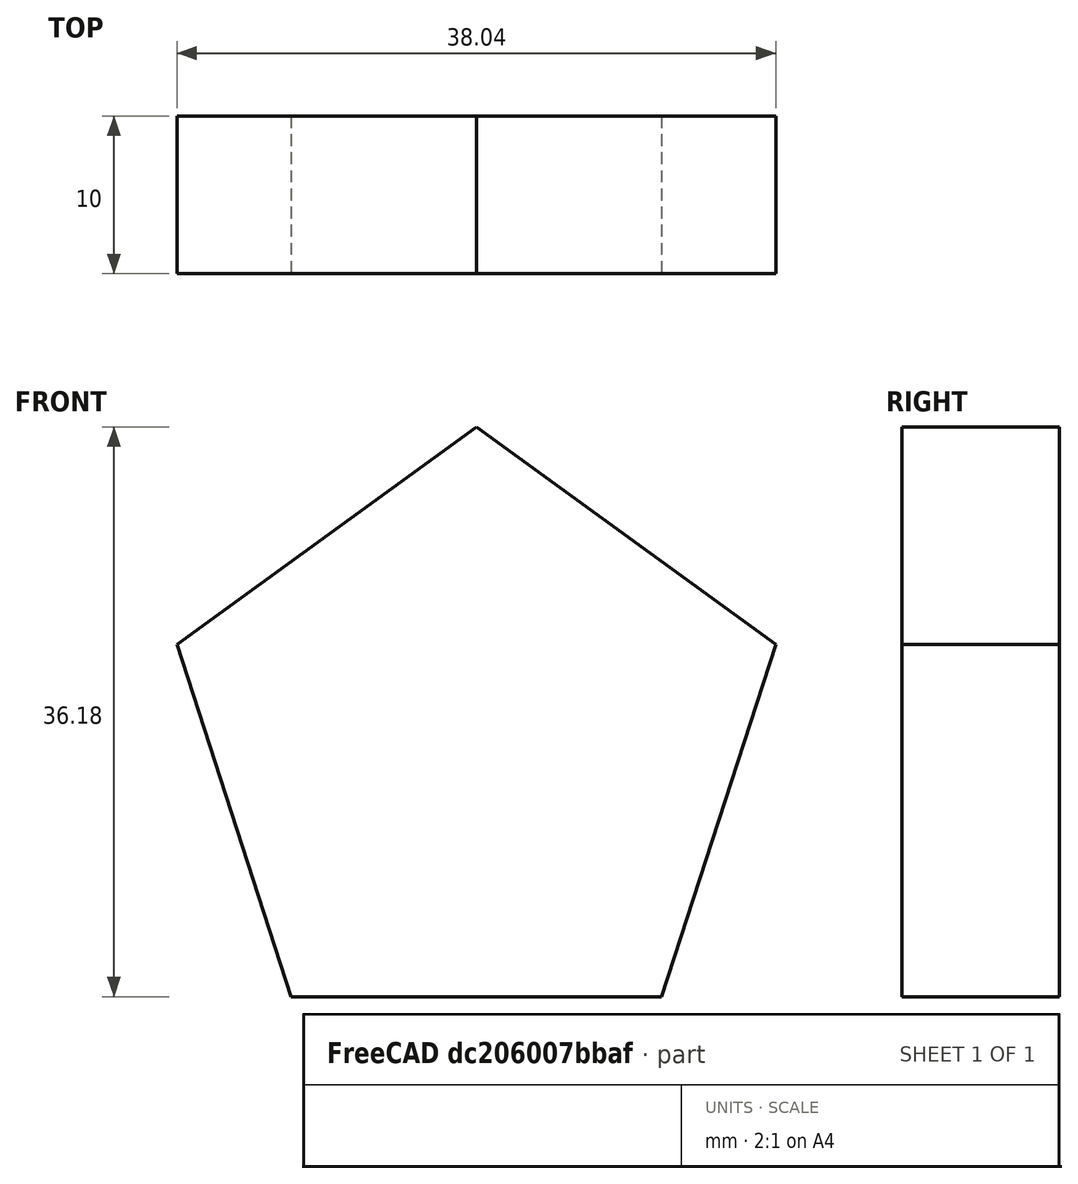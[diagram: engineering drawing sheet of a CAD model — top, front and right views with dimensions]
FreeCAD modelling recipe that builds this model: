
FCSTD DOCUMENT  (FreeCAD 2023.521R14555 (Git shallow))
Label: Penta
License: All rights reserved
objects: PartDesign::CoordinateSystem×2, Sketcher::SketchObject×1, PartDesign::Pad×1, PartDesign::Body×1, App::Part×1, App::Link×1
note: 8 computed .brp shape members not serialized (recipe doc carries the construction recipe); baked Part::Feature solids carry a one-line shape summary decoded from their .brp
EXTERNAL_REF file=Main_board.FCStd obj=Spreadsheet

FEATURE [PartDesign::CoordinateSystem] LCS_0
  AttacherType = Attacher::AttachEngine3D
  AttachmentSupport = -> [X_Axis]
  InvalidShape = false
  MapMode = 2
  Support = -> [X_Axis]
  TreeRank = 3
  ValidateShape = false
FEATURE [PartDesign::CoordinateSystem] LCS_0001
  AttacherType = Attacher::AttachEngine3D
  AttachmentSupport = -> [X_Axis001]
  InvalidShape = false
  MapMode = 2
  Support = -> [X_Axis001]
  TreeRank = 21
  ValidateShape = false
FEATURE [Sketcher::SketchObject] Sketch
  ArcFitTolerance = 1e-06
  AttachmentSupport = -> [XZ_Plane001]
  ExternalBSplineMaxDegree = 5
  ExternalBSplineTolerance = 0.0001
  FullyConstrained = true
  InternalTolerance = 1e-06
  InvalidShape = false
  MakeInternals = false
  MapMode = 5
  Placement = pos=(0,0,0) rot=(1,0,0;1.5708rad)
  Support = -> [XZ_Plane001]
  TreeRank = 23
  ValidateShape = false
  expr: Constraints[15] = <<dims>>.PS
  sketch-geometry (6):
    g0: LineSegment StartX=3.1e-15 StartY=20 StartZ=0 EndX=-19.0211 EndY=6.18034 EndZ=0
    g1: LineSegment StartX=-19.0211 StartY=6.18034 StartZ=0 EndX=-11.7557 EndY=-16.1803 EndZ=0
    g2: LineSegment StartX=-11.7557 StartY=-16.1803 StartZ=0 EndX=11.7557 EndY=-16.1803 EndZ=0
    g3: LineSegment StartX=11.7557 StartY=-16.1803 StartZ=0 EndX=19.0211 EndY=6.18034 EndZ=0
    g4: LineSegment StartX=19.0211 StartY=6.18034 StartZ=0 EndX=3.6e-15 EndY=20 EndZ=0
    g5: Circle [constr] CenterX=0 CenterY=0 CenterZ=0 NormalX=0 NormalY=0 NormalZ=1 AngleXU=0 Radius=20
  constraints (14):
    c: Coincident(g0,g1)
    c: Coincident(g1,g2)
    c: Coincident(g2,g3)
    c: Coincident(g3,g4)
    c: Coincident(g4,g0)
    c: Equal(g0, g1-g4) x4
    c: PointOnObject(g0,g5)
    c: PointOnObject(g1,g5)
    c: PointOnObject(g2,g5)
    c: PointOnObject(g3,g5)
    c: PointOnObject(g4,g5)
    c: Coincident(g5,g-1)
    c: Diameter(g5) = 40
    c: Horizontal(g2)
FEATURE [PartDesign::Pad] Pad
  AddSubType = 0
  AlongSketchNormal = false
  AutoTaperInnerAngle = true
  CheckUpToFaceLimits = true
  ClaimChildren = false
  Direction = (0,-1,2e-16)
  Fit = 0
  FitJoin = 0
  InnerFit = 0
  InnerFitJoin = 0
  InvalidShape = false
  Length = 10
  Length2 = 10
  Linearize = true
  NewSolid = false
  Profile = -> Sketch
  ReferenceAxis = -> Sketch [N_Axis]
  Suppress = false
  TaperInnerAngle = 0
  TaperInnerAngleRev = 0
  TreeRank = 24
  Type = 0
  ValidateShape = true
  _ProfileBasedVersion = 1
FEATURE [PartDesign::Body] Body
  AutoGroupSolids = false
  ClaimAllChildren = false
  ExportMode = 0
  Group = -> [LCS_0001,Sketch,Pad]
  InvalidShape = false
  Origin = -> Origin001
  Tip = -> Pad
  TreeRank = 22
  ValidateShape = false
  _ExportChildren = -> [LCS_0001,Pad]
  _GroupVersion = 1
FEATURE [App::Part] Penta
  ClaimAllChildren = false
  ExportMode = 1
  Group = -> [LCS_0,Body]
  Origin = -> Origin
  TreeRank = 11
  _ExportChildren = -> [LCS_0,Body]
  _GroupVersion = 1
FEATURE [App::Link] Link  label="dims"
  AutoLinkLabel = true
  AutoPlacement = true
  LinkedObject = -> <external Main_board.FCStd>#Spreadsheet
  SyncGroupVisibility = false
  TreeRank = 26
  _LinkVersion = 1

RESOLVED EXTERNAL PARTS (link-assembly join: the EXTERNAL_REF files above that resolve inside this repo's crawl, each included once):
---- part Main_board.FCStd = doc fcstd_18a85a5c1fb4 ----
FCSTD DOCUMENT  (FreeCAD 2023.521R14555 (Git shallow))
Label: Main_board
License: All rights reserved
objects: PartDesign::CoordinateSystem×5, Sketcher::SketchObject×2, PartDesign::Pad×1, Spreadsheet::Sheet×1, PartDesign::Body×1, App::Part×1
note: 13 computed .brp shape members not serialized (recipe doc carries the construction recipe); baked Part::Feature solids carry a one-line shape summary decoded from their .brp

FEATURE [Sketcher::SketchObject] Sketch
  ArcFitTolerance = 1e-06
  AttachmentSupport = -> [XZ_Plane]
  ExternalBSplineMaxDegree = 5
  ExternalBSplineTolerance = 0.0001
  FullyConstrained = true
  InternalTolerance = 1e-06
  InvalidShape = false
  MakeInternals = false
  MapMode = 5
  Placement = pos=(0,0,0) rot=(1,0,0;1.5708rad)
  Support = -> [XZ_Plane]
  TreeRank = 11
  ValidateShape = false
  expr: Constraints[48] = <<dims>>.HS
  sketch-geometry (31):
    g0: LineSegment StartX=-40 StartY=19 StartZ=0 EndX=-21.8135 EndY=50.5 EndZ=0
    g1: LineSegment StartX=-21.8135 StartY=50.5 StartZ=0 EndX=-58.1865 EndY=50.5 EndZ=0
    g2: LineSegment StartX=-58.1865 StartY=50.5 StartZ=0 EndX=-40 EndY=19 EndZ=0
    g3: Circle [constr] CenterX=-40 CenterY=40 CenterZ=0 NormalX=0 NormalY=0 NormalZ=1 AngleXU=0 Radius=21
    g4: LineSegment StartX=40 StartY=-19 StartZ=0 EndX=21.8135 EndY=-50.5 EndZ=0
    g5: LineSegment StartX=21.8135 StartY=-50.5 StartZ=0 EndX=58.1865 EndY=-50.5 EndZ=0
    g6: LineSegment StartX=58.1865 StartY=-50.5 StartZ=0 EndX=40 EndY=-19 EndZ=0
    g7: Circle [constr] CenterX=40 CenterY=-40 CenterZ=0 NormalX=0 NormalY=0 NormalZ=1 AngleXU=0 Radius=21
    g8: LineSegment StartX=27.6565 StartY=23.0106 StartZ=0 EndX=52.3435 EndY=23.0106 EndZ=0
    g9: LineSegment StartX=52.3435 StartY=23.0106 StartZ=0 EndX=59.9722 EndY=46.4894 EndZ=0
    g10: LineSegment StartX=59.9722 StartY=46.4894 StartZ=0 EndX=40 EndY=61 EndZ=0
    g11: LineSegment StartX=40 StartY=61 StartZ=0 EndX=20.0278 EndY=46.4894 EndZ=0
    g12: LineSegment StartX=20.0278 StartY=46.4894 StartZ=0 EndX=27.6565 EndY=23.0106 EndZ=0
    g13: Circle [constr] CenterX=40 CenterY=40 CenterZ=0 NormalX=0 NormalY=0 NormalZ=1 AngleXU=0 Radius=21
    g14: LineSegment StartX=-21.8135 StartY=-29.5 StartZ=0 EndX=-40 EndY=-19 EndZ=0
    g15: LineSegment StartX=-40 StartY=-19 StartZ=0 EndX=-58.1865 EndY=-29.5 EndZ=0
    g16: LineSegment StartX=-58.1865 StartY=-29.5 StartZ=0 EndX=-58.1865 EndY=-50.5 EndZ=0
    g17: LineSegment StartX=-58.1865 StartY=-50.5 StartZ=0 EndX=-40 EndY=-61 EndZ=0
    g18: LineSegment StartX=-40 StartY=-61 StartZ=0 EndX=-21.8135 EndY=-50.5 EndZ=0
    g19: LineSegment StartX=-21.8135 StartY=-50.5 StartZ=0 EndX=-21.8135 EndY=-29.5 EndZ=0
    g20: Circle [constr] CenterX=-40 CenterY=-40 CenterZ=0 NormalX=0 NormalY=0 NormalZ=1 AngleXU=0 Radius=21
    g21: Circle CenterX=0 CenterY=0 CenterZ=0 NormalX=0 NormalY=0 NormalZ=1 AngleXU=0 Radius=21
    g22: LineSegment [constr] StartX=-40 StartY=40 StartZ=0 EndX=40 EndY=40 EndZ=0
    g23: LineSegment [constr] StartX=40 StartY=40 StartZ=0 EndX=40 EndY=-40 EndZ=0
    g24: LineSegment [constr] StartX=40 StartY=-40 StartZ=0 EndX=-40 EndY=-40 EndZ=0
    g25: LineSegment [constr] StartX=-40 StartY=-40 StartZ=0 EndX=-40 EndY=40 EndZ=0
    g26: LineSegment StartX=-70 StartY=-70 StartZ=0 EndX=-70 EndY=70 EndZ=0
    g27: LineSegment StartX=-70 StartY=70 StartZ=0 EndX=70 EndY=70 EndZ=0
    g28: LineSegment StartX=70 StartY=70 StartZ=0 EndX=70 EndY=-70 EndZ=0
    g29: LineSegment StartX=70 StartY=-70 StartZ=0 EndX=-70 EndY=-70 EndZ=0
    g30: GeomPoint [constr] X=0 Y=0 Z=0
  constraints (77):
    c: Coincident(g0,g1)
    c: Coincident(g1,g2)
    c: Coincident(g2,g0)
    c: Equal(g0,g1)
    c: Equal(g0,g2)
    c: PointOnObject(g0,g3)
    c: PointOnObject(g1,g3)
    c: PointOnObject(g2,g3)
    c: Coincident(g4,g5)
    c: Coincident(g5,g6)
    c: Coincident(g6,g4)
    c: Equal(g4,g5)
    c: Equal(g4,g6)
    c: PointOnObject(g4,g7)
    c: PointOnObject(g5,g7)
    c: PointOnObject(g6,g7)
    c: Coincident(g8,g9)
    c: Coincident(g9,g10)
    c: Coincident(g10,g11)
    c: Coincident(g11,g12)
    c: Coincident(g12,g8)
    c: Equal(g8, g9-g12) x4
    c: PointOnObject(g8,g13)
    c: PointOnObject(g9,g13)
    c: PointOnObject(g10,g13)
    c: PointOnObject(g11,g13)
    c: PointOnObject(g12,g13)
    c: Coincident(g14,g15)
    c: Coincident(g15,g16)
    c: Coincident(g16,g17)
    c: Coincident(g17,g18)
    c: Coincident(g18,g19)
    c: Coincident(g19,g14)
    c: Equal(g14, g15-g19) x5
    c: PointOnObject(g14,g20)
    c: PointOnObject(g15,g20)
    c: PointOnObject(g16,g20)
    c: PointOnObject(g17,g20)
    c: PointOnObject(g18,g20)
    c: PointOnObject(g19,g20)
    c: Coincident(g21,g-1)
    c: Diameter(g13) = 42
    c: Horizontal(g8)
    c: Equal(g13,g7)
    c: Equal(g7,g20)
    c: Equal(g20,g3)
    c: Vertical(g19)
    c: Horizontal(g5)
    c: Horizontal(g1)
    c: Coincident(g22,g23)
    c: Coincident(g23,g24)
    c: Coincident(g24,g25)
    c: Coincident(g25,g22)
    c: Horizontal(g22)
    c: Horizontal(g24)
    c: Vertical(g23)
    c: Vertical(g25)
    c: Coincident(g22,g3)
    c: Coincident(g23,g7)
    c: Coincident(g22,g13)
    c: Coincident(g24,g20)
    c: Symmetric(g24,g22,g21)
    c: Equal(g23,g24)
    c: DistanceY(g23,g23) = 80
    c: Coincident(g26,g27)
    c: Coincident(g27,g28)
    c: Coincident(g28,g29)
    c: Coincident(g29,g26)
    c: Horizontal(g27)
    c: Horizontal(g29)
    c: Vertical(g26)
    c: Vertical(g28)
    c: Symmetric(g27,g26,g30)
    c: Coincident(g30,g21)
    c: Equal(g28,g29)
    c: DistanceY(g28,g28) = 140
    c: Equal(g21,g13)
FEATURE [PartDesign::Pad] Pad
  AddSubType = 0
  AlongSketchNormal = false
  AutoTaperInnerAngle = true
  CheckUpToFaceLimits = true
  ClaimChildren = false
  Direction = (0,-1,-2e-16)
  Fit = 0
  FitJoin = 0
  InnerFit = 0
  InnerFitJoin = 0
  InvalidShape = false
  Length = 4
  Length2 = 10
  Linearize = true
  NewSolid = false
  Profile = -> Sketch
  ReferenceAxis = -> Sketch [N_Axis]
  Suppress = false
  TaperInnerAngle = 0
  TaperInnerAngleRev = 0
  TreeRank = 12
  Type = 0
  ValidateShape = true
  _ProfileBasedVersion = 1
FEATURE [PartDesign::CoordinateSystem] Local_CS  label="Triangle0"
  AttacherType = Attacher::AttachEngine3D
  AttachmentSupport = -> [Pad]
  InvalidShape = false
  MapMode = 13
  Placement = pos=(-40,-4,40) rot=(1,0,0;1.5708rad)
  Support = -> [Pad]
  TreeRank = 16
  ValidateShape = false
FEATURE [PartDesign::CoordinateSystem] Local_CS002  label="Triangle1"
  AttacherType = Attacher::AttachEngine3D
  AttachmentOffset = pos=(0,0,0) rot=(0,0,1;3.14159rad)
  AttachmentSupport = -> [Pad]
  InvalidShape = false
  MapMode = 13
  Placement = pos=(40,-4,-40) rot=(0,-0.707107,0.707107;3.14159rad)
  Support = -> [Pad]
  TreeRank = 21
  ValidateShape = false
FEATURE [PartDesign::CoordinateSystem] Local_CS003  label="Circle"
  AttacherType = Attacher::AttachEngine3D
  AttachmentSupport = -> [Pad]
  InvalidShape = false
  MapMode = 11
  Placement = pos=(0,-4,-9e-16) rot=(0.57735,-0.57735,0.57735;2.0944rad)
  Support = -> [Pad]
  TreeRank = 22
  ValidateShape = false
FEATURE [Spreadsheet::Sheet] Spreadsheet  label="dims"
  PythonMode = false
  ShowCells = 0
  TreeRank = 25
  cells = A1=Part SIze; B1(PS)==40mm; A2=Gap; B2==2mm; A3=Hole Size; B3(HS)==B1 + B2
FEATURE [Sketcher::SketchObject] Sketch001
  ArcFitTolerance = 1e-06
  AttachmentSupport = -> [Pad]
  ExternalBSplineMaxDegree = 5
  ExternalBSplineTolerance = 0.0001
  ExternalGeometry = -> [Pad]
  FullyConstrained = true
  InternalTolerance = 1e-06
  InvalidShape = false
  MakeInternals = false
  MapMode = 5
  Placement = pos=(0,-4,-9e-16) rot=(1,0,0;1.5708rad)
  Support = -> [Pad]
  TreeRank = 26
  ValidateShape = false
  sketch-geometry (2):
    g0: Circle CenterX=40 CenterY=40 CenterZ=0 NormalX=0 NormalY=0 NormalZ=1 AngleXU=0 Radius=21
    g1: Circle CenterX=-40 CenterY=-40 CenterZ=0 NormalX=0 NormalY=0 NormalZ=1 AngleXU=0 Radius=21
  constraints (6):
    c: PointOnObject(g-4,g0)
    c: PointOnObject(g-3,g0)
    c: PointOnObject(g-3,g0)
    c: PointOnObject(g-5,g1)
    c: PointOnObject(g-6,g1)
    c: PointOnObject(g-6,g1)
FEATURE [PartDesign::Body] Body
  AutoGroupSolids = false
  ClaimAllChildren = false
  ExportMode = 0
  Group = -> [Sketch,Pad,Sketch001]
  InvalidShape = false
  Origin = -> Origin
  Tip = -> Pad
  TreeRank = 10
  ValidateShape = false
  _ExportChildren = -> [Pad,Sketch001]
  _GroupVersion = 1
FEATURE [PartDesign::CoordinateSystem] Local_CS004  label="Penta"
  AttacherType = Attacher::AttachEngine3D
  AttachmentSupport = -> [Sketch001]
  InvalidShape = false
  MapMode = 11
  Placement = pos=(40,-4,40) rot=(-0.57735,0.57735,-0.57735;4.18879rad)
  Support = -> [Sketch001]
  TreeRank = 23
  ValidateShape = false
FEATURE [PartDesign::CoordinateSystem] Local_CS005  label="Hex"
  AttacherType = Attacher::AttachEngine3D
  AttachmentSupport = -> [Sketch001]
  InvalidShape = false
  MapMode = 11
  Placement = pos=(-40,-4,-40) rot=(-0.57735,0.57735,-0.57735;4.18879rad)
  Support = -> [Sketch001]
  TreeRank = 24
  ValidateShape = false
FEATURE [App::Part] Part
  ClaimAllChildren = false
  ExportMode = 1
  Group = -> [Body,Local_CS,Local_CS002,Local_CS003,Local_CS004,Local_CS005]
  Origin = -> Origin001
  TreeRank = 15
  _ExportChildren = -> [Body,Local_CS,Local_CS002,Local_CS003,Local_CS004,Local_CS005]
  _GroupVersion = 1
